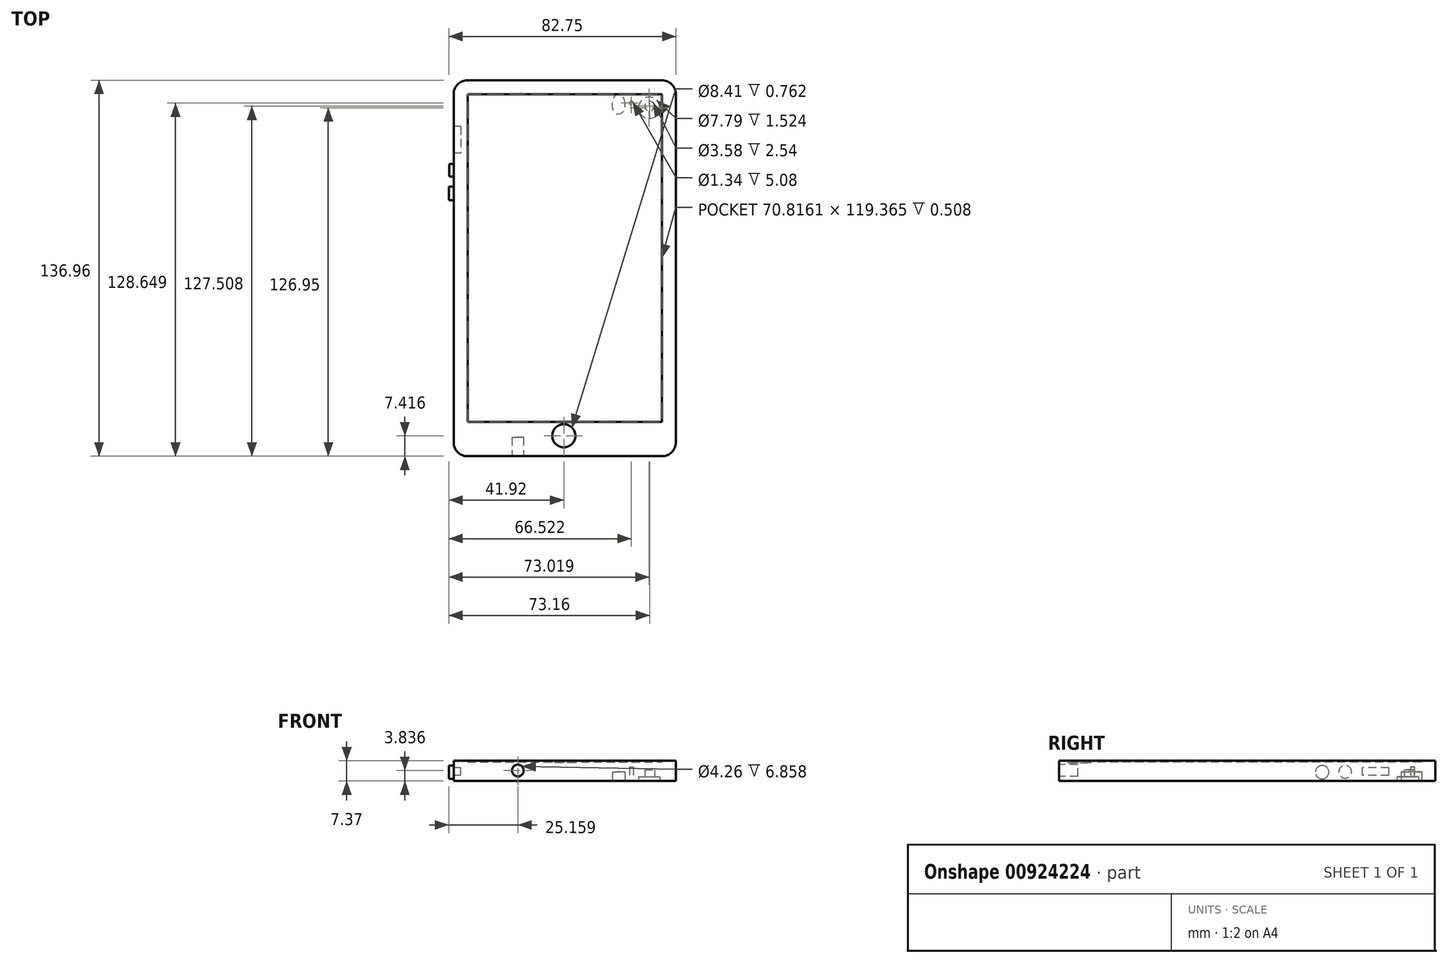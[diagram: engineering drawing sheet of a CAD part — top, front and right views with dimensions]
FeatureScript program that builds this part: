
annotation { "Feature Type Name" : "Feature", "Feature Type Description" : "" }
export const myFeature = defineFeature(function(context is Context, id is Id, definition is map)
    precondition{}
    {
        {
            var Q0;
            Q0=qCreatedBy(makeId("Top.planeOp"),FACE);
            var sketch = newSketch(context, id + "F0", { "sketchPlane" : qUnion([Q0])});
            skLineSegment(sketch, "E0.bottom", {"start": v(-40.14, 64) * mm, "end": v(40.83, 64) * mm});
            skLineSegment(sketch, "E0.top", {"start": v(-40.14, -72.97) * mm, "end": v(40.83, -72.97) * mm});
            skLineSegment(sketch, "E0.left", {"start": v(-40.14, 64) * mm, "end": v(-40.14, -72.97) * mm});
            skLineSegment(sketch, "E0.right", {"start": v(40.83, 64) * mm, "end": v(40.83, -72.97) * mm});
            skSolve(sketch);
        }
        {
            var Q0;
            Q0 = qSketchRegion(id + "F0", true);
            extrude(context, id + "F1", {"entities" : qUnion([Q0]), "depth" : 7.37 * mm, "offsetDistance" : 25.4 * mm});
        }
        {
            var Q0;
            Q0=makeQuery(id+"F1.opExtrude","SWEPT_EDGE",EDGE,{"disambiguationData":[OSD([sQuery(id+"F0.wireOp",EDGE,"E0.bottom"),sQuery(id+"F0.wireOp",EDGE,"E0.left")])]});
            var Q1;
            Q1=makeQuery(id+"F1.opExtrude","SWEPT_EDGE",EDGE,{"disambiguationData":[OSD([sQuery(id+"F0.wireOp",EDGE,"E0.bottom"),sQuery(id+"F0.wireOp",EDGE,"E0.right")])]});
            var Q2;
            Q2=makeQuery(id+"F1.opExtrude","SWEPT_EDGE",EDGE,{"disambiguationData":[OSD([sQuery(id+"F0.wireOp",EDGE,"E0.top"),sQuery(id+"F0.wireOp",EDGE,"E0.right")])]});
            var Q3;
            Q3=makeQuery(id+"F1.opExtrude","SWEPT_EDGE",EDGE,{"disambiguationData":[OSD([sQuery(id+"F0.wireOp",EDGE,"E0.top"),sQuery(id+"F0.wireOp",EDGE,"E0.left")])]});
            fillet(context, id + "F2", {"entities" : qUnion([Q0, Q1, Q2, Q3]), "radius" : 5.08 * mm, "tangentPropagation" : true, "allowEdgeOverflow" : false});
        }
        {
            var Q0;
            Q0=makeQuery(id+"F1.opExtrude","CAP_FACE",FACE,{"disambiguationData":[OSD([sQuery(id+"F0.wireOp",EDGE,"E0.bottom"),sQuery(id+"F0.wireOp",EDGE,"E0.top"),sQuery(id+"F0.wireOp",EDGE,"E0.left"),sQuery(id+"F0.wireOp",EDGE,"E0.right")])],"isStart":false});
            var sketch = newSketch(context, id + "F3", { "sketchPlane" : qUnion([Q0])});
            skLineSegment(sketch, "E1.bottom", {"start": v(-35.06, 58.91) * mm, "end": v(35.76, 58.91) * mm});
            skLineSegment(sketch, "E1.top", {"start": v(-35.06, -60.45) * mm, "end": v(35.76, -60.45) * mm});
            skLineSegment(sketch, "E1.left", {"start": v(-35.06, 58.91) * mm, "end": v(-35.06, -60.45) * mm});
            skLineSegment(sketch, "E1.right", {"start": v(35.76, 58.91) * mm, "end": v(35.76, -60.45) * mm});
            skSolve(sketch);
        }
        {
            var Q0;
            Q0=makeQuery(id+"F3.imprint","IMPRINT",FACE,{"disambiguationData":[TD([[makeQuery(id+"F3.imprint","IMPRINT",EDGE,{"derivedFrom":sQuery(id+"F3.wireOp",EDGE,"E1.bottom")}),-1.0]])]});
            extrude(context, id + "F4", {"entities" : qUnion([Q0]), "operationType" : NewBodyOperationType.REMOVE, "oppositeDirection" : true, "depth" : 0.5 * mm, "offsetDistance" : 25.4 * mm});
        }
        {
            var Q0;
            Q0=makeQuery(id+"F1.opExtrude","CAP_FACE",FACE,{"disambiguationData":[OSD([sQuery(id+"F0.wireOp",EDGE,"E0.bottom"),sQuery(id+"F0.wireOp",EDGE,"E0.top"),sQuery(id+"F0.wireOp",EDGE,"E0.left"),sQuery(id+"F0.wireOp",EDGE,"E0.right")])],"isStart":false});
            var sketch = newSketch(context, id + "F5", { "sketchPlane" : qUnion([Q0])});
            skCircle(sketch, "E2", {"center": v(0, -65.55) * mm, "radius": 4.2 * mm});
            skSolve(sketch);
        }
        {
            var Q0;
            Q0 = qSketchRegion(id + "F5", true);
            extrude(context, id + "F6", {"entities" : qUnion([Q0]), "operationType" : NewBodyOperationType.REMOVE, "oppositeDirection" : true, "depth" : 0.76 * mm, "offsetDistance" : 25.4 * mm});
        }
        {
            var Q0;
            Q0=makeQuery(id+"F1.opExtrude","SWEPT_FACE",FACE,{"disambiguationData":[OSD([sQuery(id+"F0.wireOp",EDGE,"E0.left")])]});
            var sketch = newSketch(context, id + "F7", { "sketchPlane" : qUnion([Q0])});
            skLineSegment(sketch, "E3.bottom", {"start": v(-47.19, 2.03) * mm, "end": v(-37.48, 2.03) * mm});
            skLineSegment(sketch, "E3.top", {"start": v(-47.19, 4.86) * mm, "end": v(-37.48, 4.86) * mm});
            skLineSegment(sketch, "E3.left", {"start": v(-47.19, 2.03) * mm, "end": v(-47.19, 4.86) * mm});
            skLineSegment(sketch, "E3.right", {"start": v(-37.48, 2.03) * mm, "end": v(-37.48, 4.86) * mm});
            skSolve(sketch);
        }
        {
            var Q0;
            Q0 = qSketchRegion(id + "F7", true);
            extrude(context, id + "F8", {"entities" : qUnion([Q0]), "operationType" : NewBodyOperationType.REMOVE, "oppositeDirection" : true, "depth" : 2.54 * mm, "offsetDistance" : 25.4 * mm});
        }
        {
            var Q0;
            Q0=makeQuery(id+"F1.opExtrude","SWEPT_FACE",FACE,{"disambiguationData":[OSD([sQuery(id+"F0.wireOp",EDGE,"E0.left")])]});
            var sketch = newSketch(context, id + "F9", { "sketchPlane" : qUnion([Q0])});
            skCircle(sketch, "E4", {"center": v(-31.2, 3.38) * mm, "radius": 2.32 * mm});
            skSolve(sketch);
        }
        {
            var Q0;
            Q0 = qSketchRegion(id + "F9", true);
            extrude(context, id + "F10", {"entities" : qUnion([Q0]), "operationType" : NewBodyOperationType.ADD, "depth" : 1.63 * mm, "offsetDistance" : 25.4 * mm});
        }
        {
            var Q0;
            Q0=makeQuery(id+"F1.opExtrude","SWEPT_FACE",FACE,{"disambiguationData":[OSD([sQuery(id+"F0.wireOp",EDGE,"E0.left")])]});
            var sketch = newSketch(context, id + "F11", { "sketchPlane" : qUnion([Q0])});
            skCircle(sketch, "E5", {"center": v(-22.8, 3.23) * mm, "radius": 2.45 * mm});
            skSolve(sketch);
        }
        {
            var Q0;
            Q0 = qSketchRegion(id + "F11", true);
            extrude(context, id + "F12", {"entities" : qUnion([Q0]), "operationType" : NewBodyOperationType.ADD, "depth" : 1.78 * mm, "offsetDistance" : 25.4 * mm});
        }
        {
            var Q0;
            Q0=makeQuery(id+"F1.opExtrude","CAP_FACE",FACE,{"disambiguationData":[OSD([sQuery(id+"F0.wireOp",EDGE,"E0.bottom"),sQuery(id+"F0.wireOp",EDGE,"E0.top"),sQuery(id+"F0.wireOp",EDGE,"E0.left"),sQuery(id+"F0.wireOp",EDGE,"E0.right")])],"isStart":true});
            var sketch = newSketch(context, id + "F13", { "sketchPlane" : qUnion([Q0])});
            skLineSegment(sketch, "E6", {"start": v(40.83, -41.83) * mm, "end": v(-40.14, -41.83) * mm});
            skSolve(sketch);
        }
        {
            var Q0;
            {var subQ6=sQuery(id+"F13.wireOp",EDGE,"E6");Q0=makeQuery(id+"F13.imprint","IMPRINT",FACE,{"disambiguationData":[TD([[makeQuery(id+"F13.imprint","IMPRINT",EDGE,{"derivedFrom":subQ6}),1.0]])]});}
            var sketch = newSketch(context, id + "F14", { "sketchPlane" : qUnion([Q0])});
            skCircle(sketch, "E7", {"center": v(31.1, -53.98) * mm, "radius": 3.9 * mm});
            skSolve(sketch);
        }
        {
            var Q0;
            Q0 = qSketchRegion(id + "F14", true);
            extrude(context, id + "F15", {"entities" : qUnion([Q0]), "operationType" : NewBodyOperationType.REMOVE, "oppositeDirection" : true, "depth" : 1.52 * mm, "offsetDistance" : 25.4 * mm});
        }
        {
            var Q0;
            {var subQ6=sQuery(id+"F13.wireOp",EDGE,"E6");Q0=makeQuery(id+"F13.imprint","IMPRINT",FACE,{"disambiguationData":[TD([[makeQuery(id+"F13.imprint","IMPRINT",EDGE,{"derivedFrom":subQ6}),1.0]])]});}
            var sketch = newSketch(context, id + "F16", { "sketchPlane" : qUnion([Q0])});
            skCircle(sketch, "E8", {"center": v(31.24, -54.54) * mm, "radius": 1.79 * mm});
            skSolve(sketch);
        }
        {
            var Q0;
            Q0 = qSketchRegion(id + "F16", true);
            extrude(context, id + "F17", {"entities" : qUnion([Q0]), "operationType" : NewBodyOperationType.REMOVE, "oppositeDirection" : true, "depth" : 4.06 * mm, "offsetDistance" : 25.4 * mm});
        }
        {
            var Q0;
            {var subQ6=sQuery(id+"F13.wireOp",EDGE,"E6");Q0=makeQuery(id+"F13.imprint","IMPRINT",FACE,{"disambiguationData":[TD([[makeQuery(id+"F13.imprint","IMPRINT",EDGE,{"derivedFrom":subQ6}),1.0]])]});}
            var sketch = newSketch(context, id + "F18", { "sketchPlane" : qUnion([Q0])});
            skCircle(sketch, "E9", {"center": v(24.6, -55.68) * mm, "radius": 0.67 * mm});
            skSolve(sketch);
        }
        {
            var Q0;
            Q0 = qSketchRegion(id + "F18", true);
            extrude(context, id + "F19", {"entities" : qUnion([Q0]), "operationType" : NewBodyOperationType.REMOVE, "oppositeDirection" : true, "depth" : 5.08 * mm, "offsetDistance" : 25.4 * mm});
        }
        {
            var Q0;
            {var subQ6=sQuery(id+"F13.wireOp",EDGE,"E6");Q0=makeQuery(id+"F13.imprint","IMPRINT",FACE,{"disambiguationData":[TD([[makeQuery(id+"F13.imprint","IMPRINT",EDGE,{"derivedFrom":subQ6}),1.0]])]});}
            var sketch = newSketch(context, id + "F20", { "sketchPlane" : qUnion([Q0])});
            skFitSpline(sketch, "E10", {"points": [v(21.84, -57.12) * mm, v(21.7, -52.7) * mm, v(19.4, -51.6) * mm, v(18, -53.09) * mm, v(18.2, -57.74) * mm, v(20.14, -59.1) * mm, v(21.84, -57.12) * mm]});
            skSolve(sketch);
        }
        {
            var Q0;
            Q0 = qSketchRegion(id + "F20", true);
            extrude(context, id + "F21", {"entities" : qUnion([Q0]), "operationType" : NewBodyOperationType.REMOVE, "oppositeDirection" : true, "depth" : 3.3 * mm, "offsetDistance" : 25.4 * mm});
        }
        {
            var Q0;
            Q0=makeQuery(id+"F1.opExtrude","SWEPT_FACE",FACE,{"disambiguationData":[OSD([sQuery(id+"F0.wireOp",EDGE,"E0.top")])]});
            var sketch = newSketch(context, id + "F22", { "sketchPlane" : qUnion([Q0])});
            skCircle(sketch, "E11", {"center": v(-16.76, 3.84) * mm, "radius": 2.13 * mm});
            skSolve(sketch);
        }
        {
            var Q0;
            Q0 = qSketchRegion(id + "F22", true);
            extrude(context, id + "F23", {"entities" : qUnion([Q0]), "operationType" : NewBodyOperationType.REMOVE, "oppositeDirection" : true, "depth" : 6.86 * mm, "offsetDistance" : 25.4 * mm});
        }
    });
